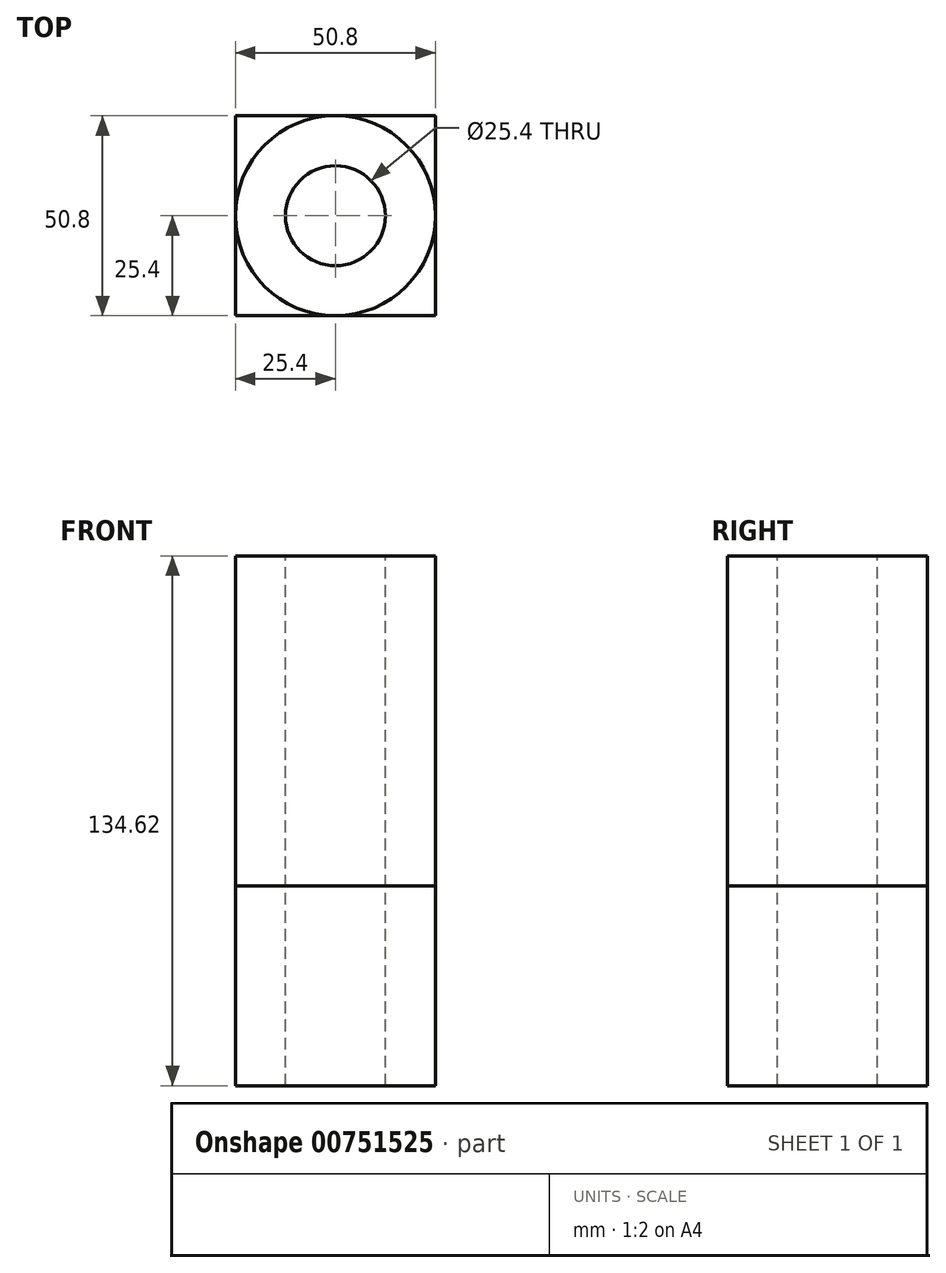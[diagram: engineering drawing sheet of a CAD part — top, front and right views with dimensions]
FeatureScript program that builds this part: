
annotation { "Feature Type Name" : "Feature", "Feature Type Description" : "" }
export const myFeature = defineFeature(function(context is Context, id is Id, definition is map)
    precondition{}
    {
        {
            var Q0;
            Q0=qCreatedBy(makeId("Top.planeOp"),FACE);
            var sketch = newSketch(context, id + "F0", { "sketchPlane" : qUnion([Q0])});
            skLineSegment(sketch, "E0.bottom", {"start": v(-50.8, 50.8) * mm, "end": v(0, 50.8) * mm});
            skLineSegment(sketch, "E0.top", {"start": v(-50.8, 0) * mm, "end": v(0, 0) * mm});
            skLineSegment(sketch, "E0.left", {"start": v(-50.8, 50.8) * mm, "end": v(-50.8, 0) * mm});
            skLineSegment(sketch, "E0.right", {"start": v(0, 50.8) * mm, "end": v(0, 0) * mm});
            skSolve(sketch);
        }
        {
            var Q0;
            Q0=makeQuery(id+"F0.imprint","IMPRINT",FACE,{"disambiguationData":[TD([[makeQuery(id+"F0.imprint","IMPRINT",EDGE,{"derivedFrom":sQuery(id+"F0.wireOp",EDGE,"E0.bottom")}),-1.0]])]});
            extrude(context, id + "F1", {"entities" : qUnion([Q0]), "oppositeDirection" : true, "depth" : 50.8 * mm, "offsetDistance" : 25.4 * mm});
        }
        {
            var Q0;
            Q0=makeQuery(id+"F1.opExtrude","CAP_FACE",FACE,{"disambiguationData":[OSD([sQuery(id+"F0.wireOp",EDGE,"E0.bottom"),sQuery(id+"F0.wireOp",EDGE,"E0.top"),sQuery(id+"F0.wireOp",EDGE,"E0.left"),sQuery(id+"F0.wireOp",EDGE,"E0.right")])],"isStart":true});
            var sketch = newSketch(context, id + "F2", { "sketchPlane" : qUnion([Q0])});
            skCircle(sketch, "E1", {"center": v(-25.4, 25.4) * mm, "radius": 25.4 * mm});
            skPoint(sketch, "E1.centerSnap0", {"position": v(-50.8, 25.4) * mm});
            skPoint(sketch, "E1.centerSnap1", {"position": v(-25.4, 50.8) * mm});
            skSolve(sketch);
        }
        {
            var Q0;
            {var subQ0=sQuery(id+"F2.wireOp",EDGE,"E1");var subQ1=makeQuery(id+"F2.imprint","INTERSECT",VERTEX,{"derivedFrom":[makeQuery(id+"F1.opExtrude","CAP_EDGE",EDGE,{"disambiguationData":[OSD([sQuery(id+"F0.wireOp",EDGE,"E0.bottom")])],"isStart":true}),subQ0]});Q0=makeQuery(id+"F2.imprint","IMPRINT",FACE,{"disambiguationData":[TD([[makeQuery(id+"F2.imprint","IMPRINT",EDGE,{"disambiguationData":[TD([[subQ1,1.0]])],"derivedFrom":subQ0}),1.0]])]});}
            extrude(context, id + "F3", {"entities" : qUnion([Q0]), "operationType" : NewBodyOperationType.ADD, "depth" : 83.82 * mm, "offsetDistance" : 25.4 * mm});
        }
        {
            var Q0;
            Q0=makeQuery(id+"F3.opExtrude","CAP_FACE",FACE,{"disambiguationData":[OSD([sQuery(id+"F2.wireOp",EDGE,"E1")])],"isStart":false});
            var sketch = newSketch(context, id + "F4", { "sketchPlane" : qUnion([Q0])});
            skCircle(sketch, "E2", {"center": v(-25.4, 25.4) * mm, "radius": 12.7 * mm});
            skSolve(sketch);
        }
        {
            var Q0;
            Q0=makeQuery(id+"F4.imprint","IMPRINT",FACE,{"disambiguationData":[TD([[makeQuery(id+"F4.imprint","IMPRINT",EDGE,{"derivedFrom":sQuery(id+"F4.wireOp",EDGE,"E2")}),1.0]])]});
            extrude(context, id + "F5", {"entities" : qUnion([Q0]), "operationType" : NewBodyOperationType.REMOVE, "oppositeDirection" : true, "depth" : 143.76 * mm, "offsetDistance" : 25.4 * mm});
        }
    });
